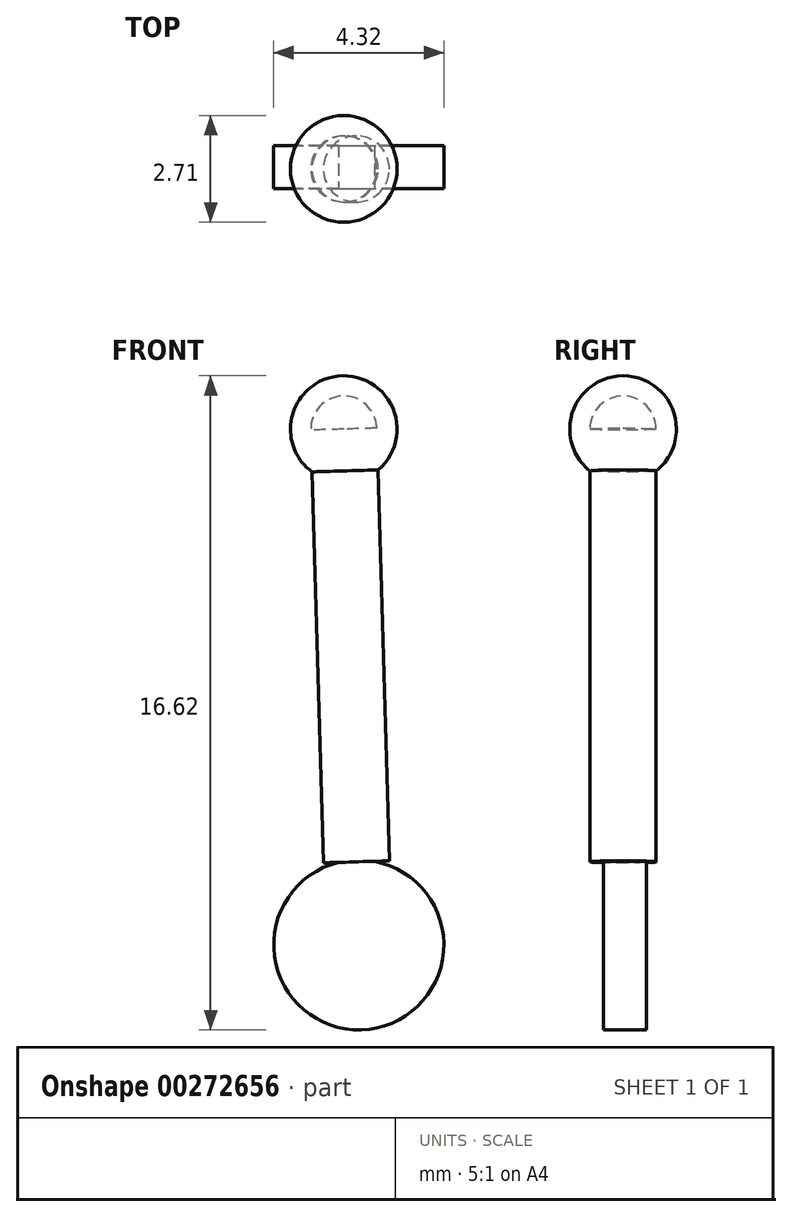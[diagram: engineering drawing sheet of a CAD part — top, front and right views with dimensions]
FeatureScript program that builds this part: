
annotation { "Feature Type Name" : "Feature", "Feature Type Description" : "" }
export const myFeature = defineFeature(function(context is Context, id is Id, definition is map)
    precondition{}
    {
        {
            var Q0;
            Q0=qCreatedBy(makeId("Front.planeOp"),FACE);
            var sketch = newSketch(context, id + "F0", { "sketchPlane" : qUnion([Q0])});
            skCircle(sketch, "E0", {"center": v(0, 0) * mm, "radius": 2.16 * mm});
            skSolve(sketch);
        }
        {
            var Q0;
            Q0 = qSketchRegion(id + "F0", true);
            extrude(context, id + "F1", {"entities" : qUnion([Q0]), "depth" : 1.09 * mm});
        }
        {
            var Q0;
            Q0=makeQuery(id+"F1.opExtrude","CAP_FACE",FACE,{"disambiguationData":[OSD([sQuery(id+"F0.wireOp",EDGE,"E0")])],"isStart":false});
            var sketch = newSketch(context, id + "F2", { "sketchPlane" : qUnion([Q0])});
            skLineSegment(sketch, "E1", {"start": v(-0.52, 2.1) * mm, "end": v(0.4, 2.12) * mm});
            skSolve(sketch);
        }
        {
            var Q0;
            {var subQ0=sQuery(id+"F2.wireOp",EDGE,"E1");Q0=makeQuery(id+"F2.imprint","IMPRINT",FACE,{"disambiguationData":[TD([[makeQuery(id+"F2.imprint","IMPRINT",EDGE,{"derivedFrom":subQ0}),1.0]])]});}
            extrude(context, id + "F3", {"entities" : qUnion([Q0]), "operationType" : NewBodyOperationType.REMOVE, "oppositeDirection" : true, "depth" : 25 * mm});
        }
        {
            var Q0;
            Q0=makeQuery(id+"F3.boolean.opBoolean","COPY",FACE,{"derivedFrom":makeQuery(id+"F3.opExtrude","SWEPT_FACE",FACE,{"disambiguationData":[OSD([sQuery(id+"F2.wireOp",EDGE,"E1")])]})});
            var sketch = newSketch(context, id + "F4", { "sketchPlane" : qUnion([Q0])});
            skCircle(sketch, "E2", {"center": v(0, -0.6) * mm, "radius": 0.84 * mm});
            skSolve(sketch);
        }
        {
            var Q0;
            Q0 = qSketchRegion(id + "F4", true);
            extrude(context, id + "F5", {"entities" : qUnion([Q0]), "operationType" : NewBodyOperationType.ADD, "depth" : 11 * mm});
        }
        {
            var Q0;
            Q0=makeQuery(id+"F5.opExtrude","CAP_FACE",FACE,{"disambiguationData":[OSD([sQuery(id+"F4.wireOp",EDGE,"E2")])],"isStart":false});
            var sketch = newSketch(context, id + "F6", { "sketchPlane" : qUnion([Q0])});
            skArc(sketch, "E3", {"start": v(0, 0.76) * mm, "mid": v(-1.36, -0.6) * mm, "end": v(0, -1.95) * mm});
            skLineSegment(sketch, "E4", {"start": v(0, 0.76) * mm, "end": v(0, -1.95) * mm});
            skSolve(sketch);
        }
        {
            var Q0;
            {var subQ0=sQuery(id+"F6.wireOp",EDGE,"E3");Q0=makeQuery(id+"F6.imprint","IMPRINT",FACE,{"disambiguationData":[TD([[makeQuery(id+"F6.imprint","IMPRINT",EDGE,{"derivedFrom":subQ0}),1.0]])]});}
            var Q1;
            Q1=sQuery(id+"F6.wireOp",EDGE,"E4");
            revolve(context, id + "F7", {"operationType" : NewBodyOperationType.ADD, "entities" : qUnion([Q0]), "axis" : qUnion([Q1]), "revolveType" : RevolveType.FULL});
        }
    });
